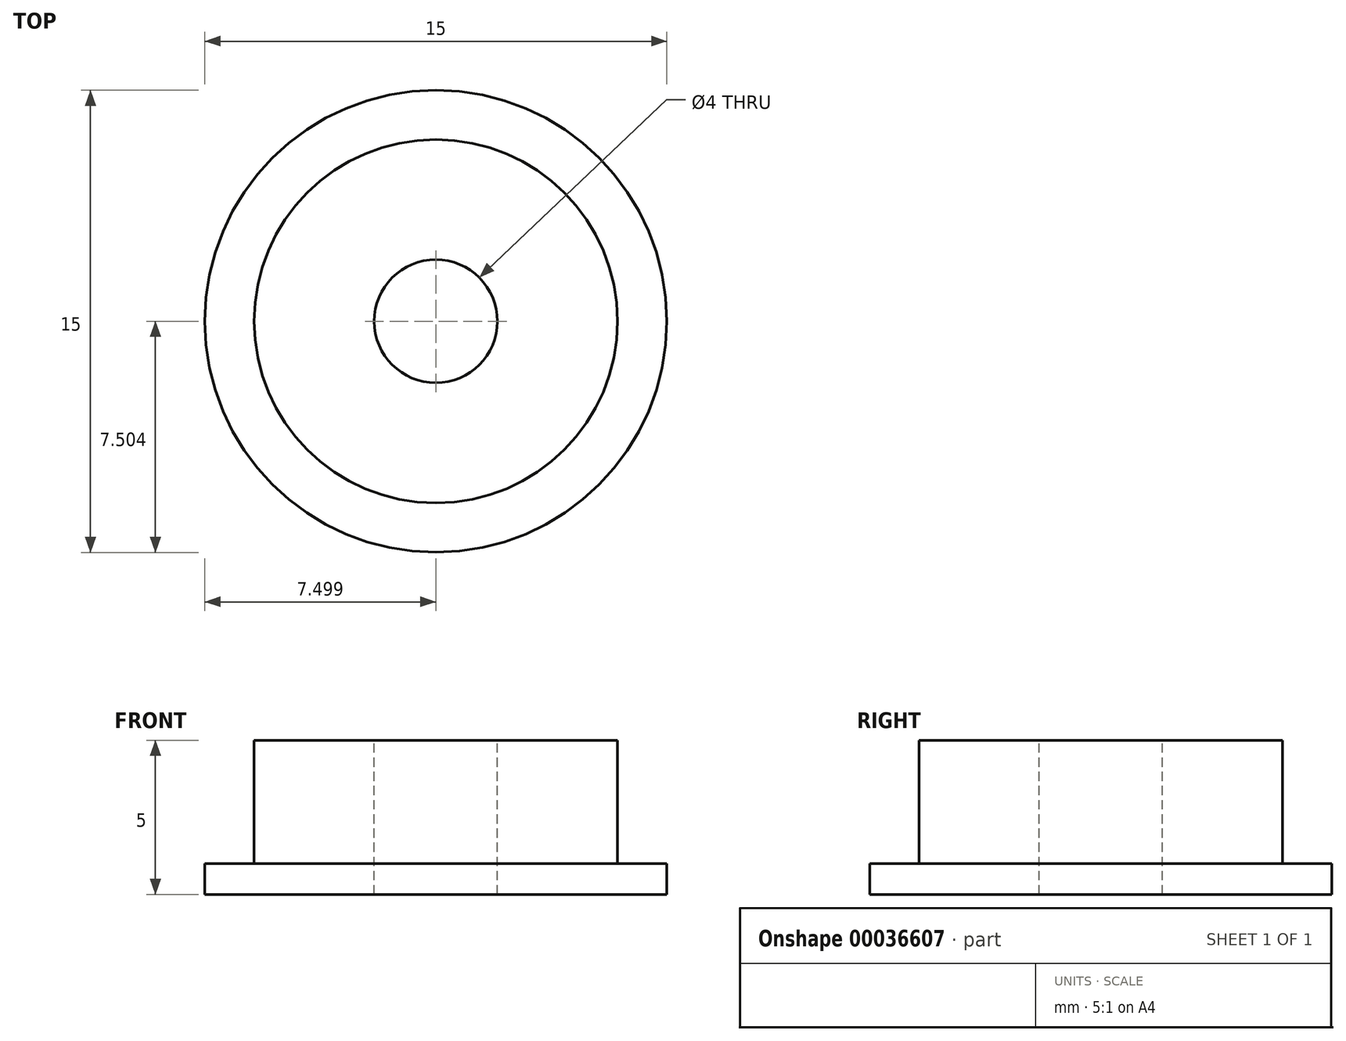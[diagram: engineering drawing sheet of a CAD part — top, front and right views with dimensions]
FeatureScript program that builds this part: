
annotation { "Feature Type Name" : "Feature", "Feature Type Description" : "" }
export const myFeature = defineFeature(function(context is Context, id is Id, definition is map)
    precondition{}
    {
        {
            var Q0;
            Q0=qCreatedBy(makeId("Top.planeOp"),FACE);
            var sketch = newSketch(context, id + "F0", { "sketchPlane" : qUnion([Q0])});
            skCircle(sketch, "E0", {"center": v(-54.88, -32.2) * mm, "radius": 7.5 * mm});
            skSolve(sketch);
        }
        {
            var Q0;
            Q0=makeQuery(id+"F0.imprint","IMPRINT",FACE,{"disambiguationData":[TD([[makeQuery(id+"F0.imprint","IMPRINT",EDGE,{"derivedFrom":sQuery(id+"F0.wireOp",EDGE,"E0")}),1.0]])]});
            extrude(context, id + "F1", {"entities" : qUnion([Q0]), "depth" : 1 * mm});
        }
        {
            var Q0;
            Q0=makeQuery(id+"F1.opExtrude","CAP_FACE",FACE,{"disambiguationData":[OSD([sQuery(id+"F0.wireOp",EDGE,"E0")])],"isStart":false});
            var sketch = newSketch(context, id + "F2", { "sketchPlane" : qUnion([Q0])});
            skCircle(sketch, "E1", {"center": v(-54.88, -32.2) * mm, "radius": 5.9 * mm});
            skSolve(sketch);
        }
        {
            var Q0;
            Q0 = qSketchRegion(id + "F2", true);
            extrude(context, id + "F3", {"entities" : qUnion([Q0]), "operationType" : NewBodyOperationType.ADD, "depth" : 4 * mm});
        }
        {
            var Q0;
            Q0=makeQuery(id+"F3.opExtrude","CAP_FACE",FACE,{"disambiguationData":[OSD([sQuery(id+"F2.wireOp",EDGE,"E1")])],"isStart":false});
            var sketch = newSketch(context, id + "F4", { "sketchPlane" : qUnion([Q0])});
            skCircle(sketch, "E2", {"center": v(-54.88, -32.2) * mm, "radius": 2 * mm});
            skSolve(sketch);
        }
        {
            var Q0;
            Q0 = qSketchRegion(id + "F4", true);
            extrude(context, id + "F5", {"entities" : qUnion([Q0]), "operationType" : NewBodyOperationType.REMOVE, "oppositeDirection" : true, "depth" : 25 * mm});
        }
    });
